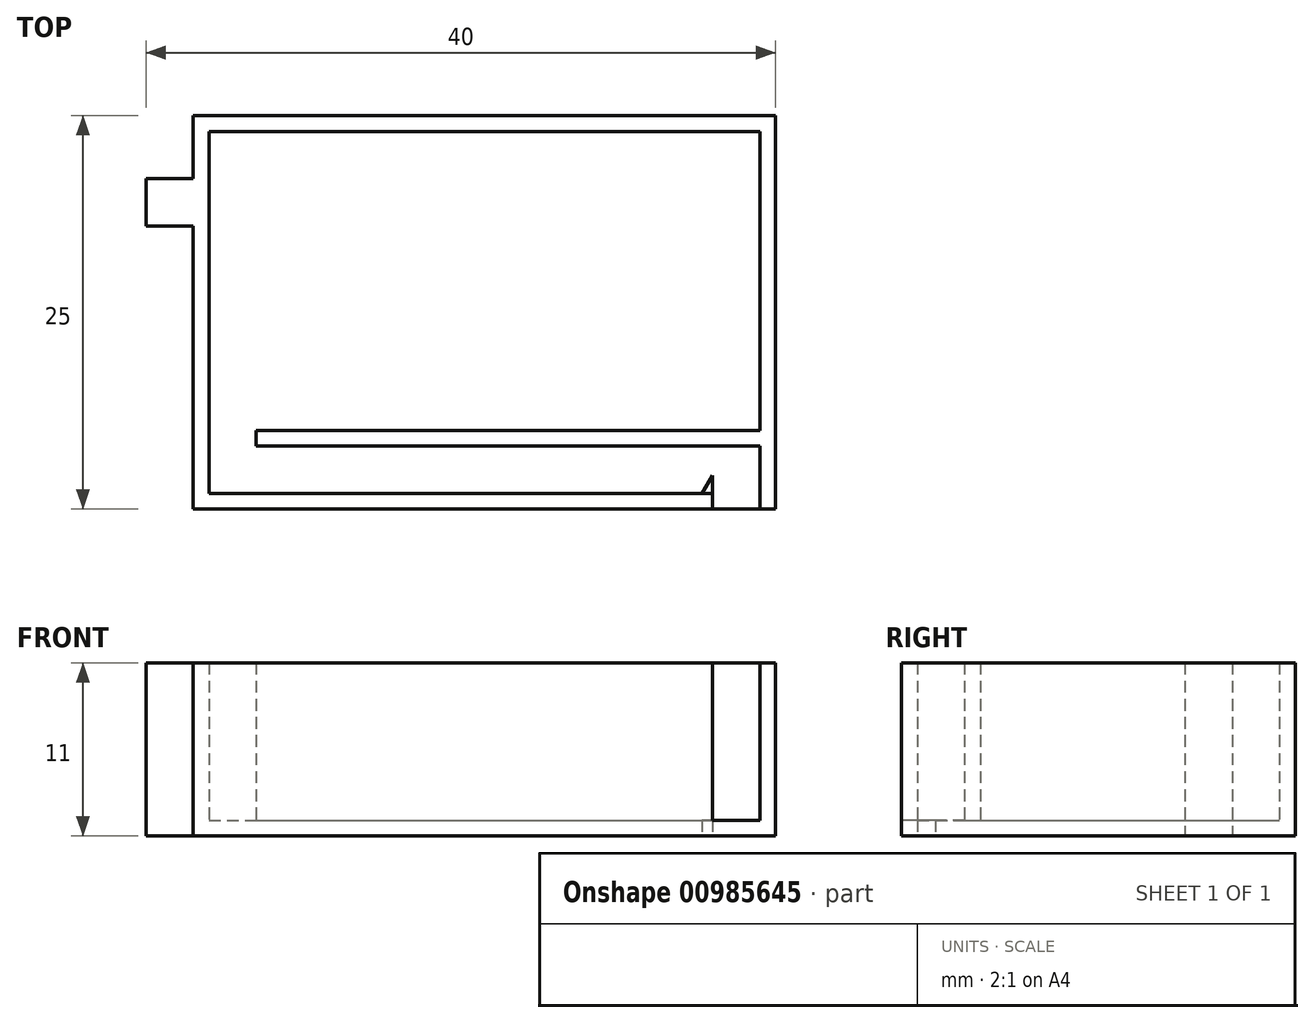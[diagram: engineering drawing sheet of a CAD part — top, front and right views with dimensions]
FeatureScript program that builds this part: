
annotation { "Feature Type Name" : "Feature", "Feature Type Description" : "" }
export const myFeature = defineFeature(function(context is Context, id is Id, definition is map)
    precondition{}
    {
        {
            var Q0;
            Q0=qCreatedBy(makeId("Top.planeOp"),FACE);
            var sketch = newSketch(context, id + "F0", { "sketchPlane" : qUnion([Q0])});
            skLineSegment(sketch, "E0.bottom", {"start": v(-20, -12.5) * mm, "end": v(20, -12.5) * mm});
            skLineSegment(sketch, "E0.top", {"start": v(-20, 12.5) * mm, "end": v(20, 12.5) * mm});
            skLineSegment(sketch, "E0.left", {"start": v(-20, -12.5) * mm, "end": v(-20, 12.5) * mm});
            skLineSegment(sketch, "E0.right", {"start": v(20, -12.5) * mm, "end": v(20, 12.5) * mm});
            skPoint(sketch, "E0.middle", {"position": v(0, 0) * mm});
            skLineSegment(sketch, "E1.bottom", {"start": v(-20, -12.5) * mm, "end": v(-17, -12.5) * mm});
            skLineSegment(sketch, "E1.top", {"start": v(-20, -10.5) * mm, "end": v(-17, -10.5) * mm});
            skLineSegment(sketch, "E1.left", {"start": v(-20, -12.5) * mm, "end": v(-20, -10.5) * mm});
            skLineSegment(sketch, "E1.right", {"start": v(-17, -12.5) * mm, "end": v(-17, -10.5) * mm});
            skLineSegment(sketch, "E2.0", {"start": v(19, -11.5) * mm, "end": v(19, 11.5) * mm});
            skLineSegment(sketch, "E2.1", {"start": v(-16, 11.5) * mm, "end": v(19, 11.5) * mm});
            skLineSegment(sketch, "E3.0", {"start": v(-17, -12.5) * mm, "end": v(-17, 12.5) * mm});
            skLineSegment(sketch, "E4.0", {"start": v(-16, -11.5) * mm, "end": v(-16, 11.5) * mm});
            skLineSegment(sketch, "E5.trimOffspring", {"start": v(-16, -11.5) * mm, "end": v(16, -11.5) * mm});
            skLineSegment(sketch, "E6", {"start": v(19, -11.5) * mm, "end": v(19, -12.5) * mm});
            skLineSegment(sketch, "E7.0", {"start": v(16, -11.5) * mm, "end": v(16, -12.5) * mm});
            skLineSegment(sketch, "E8.0", {"start": v(-20, -8.5) * mm, "end": v(-17, -8.5) * mm});
            skLineSegment(sketch, "E9.0", {"start": v(-20, -6.5) * mm, "end": v(-17, -6.5) * mm});
            skLineSegment(sketch, "E10.0", {"start": v(-20, -4.5) * mm, "end": v(-17, -4.5) * mm});
            skLineSegment(sketch, "E11.0", {"start": v(-20, -2.5) * mm, "end": v(-17, -2.5) * mm});
            skLineSegment(sketch, "E12.0", {"start": v(-20, -0.5) * mm, "end": v(-17, -0.5) * mm});
            skLineSegment(sketch, "E13.0", {"start": v(-20, 1.5) * mm, "end": v(-17, 1.5) * mm});
            skLineSegment(sketch, "E14.0", {"start": v(-20, 3.5) * mm, "end": v(-17, 3.5) * mm});
            skLineSegment(sketch, "E15.0", {"start": v(-20, 5.5) * mm, "end": v(-17, 5.5) * mm});
            skLineSegment(sketch, "E16.0", {"start": v(-20, 8.5) * mm, "end": v(-17, 8.5) * mm});
            skLineSegment(sketch, "E17.0", {"start": v(-13, -8.5) * mm, "end": v(19, -8.5) * mm});
            skLineSegment(sketch, "E18.0", {"start": v(-13, -8.5) * mm, "end": v(-13, -7.5) * mm});
            skLineSegment(sketch, "E19.0", {"start": v(-13, -7.5) * mm, "end": v(19, -7.5) * mm});
            skLineSegment(sketch, "E20", {"start": v(16, -11.5) * mm, "end": v(16, -10.36) * mm});
            skLineSegment(sketch, "E21", {"start": v(16, -10.36) * mm, "end": v(15.3, -11.5) * mm});
            skSolve(sketch);
        }
        {
            var Q0;
            {var subQ0=sQuery(id+"F0.wireOp",EDGE,"E2.1");Q0=makeQuery(id+"F0.imprint","IMPRINT",FACE,{"disambiguationData":[TD([[makeQuery(id+"F0.imprint","IMPRINT",EDGE,{"derivedFrom":subQ0}),-1.0]])]});}
            var Q1;
            {var subQ0=sQuery(id+"F0.wireOp",EDGE,"E6");Q1=makeQuery(id+"F0.imprint","IMPRINT",FACE,{"disambiguationData":[TD([[makeQuery(id+"F0.imprint","IMPRINT",EDGE,{"derivedFrom":subQ0}),-1.0]])]});}
            extrude(context, id + "F1", {"entities" : qUnion([Q0, Q1]), "depth" : 1 * mm, "offsetDistance" : 25 * mm});
        }
        {
            var Q0;
            {var subQ15=sQuery(id+"F0.wireOp",EDGE,"E0.right");Q0=makeQuery(id+"F0.imprint","IMPRINT",FACE,{"disambiguationData":[TD([[makeQuery(id+"F0.imprint","IMPRINT",EDGE,{"derivedFrom":subQ15}),1.0]])]});}
            var Q1;
            {var subQ0=sQuery(id+"F0.wireOp",EDGE,"E17.0");Q1=makeQuery(id+"F0.imprint","IMPRINT",FACE,{"disambiguationData":[TD([[makeQuery(id+"F0.imprint","IMPRINT",EDGE,{"derivedFrom":subQ0}),1.0]])]});}
            var Q2;
            {var subQ0=sQuery(id+"F0.wireOp",EDGE,"E15.0");Q2=makeQuery(id+"F0.imprint","IMPRINT",FACE,{"disambiguationData":[TD([[makeQuery(id+"F0.imprint","IMPRINT",EDGE,{"derivedFrom":subQ0}),1.0]])]});}
            extrude(context, id + "F2", {"entities" : qUnion([Q0, Q1, Q2]), "operationType" : NewBodyOperationType.ADD, "depth" : 11 * mm, "offsetDistance" : 25 * mm});
        }
    });
